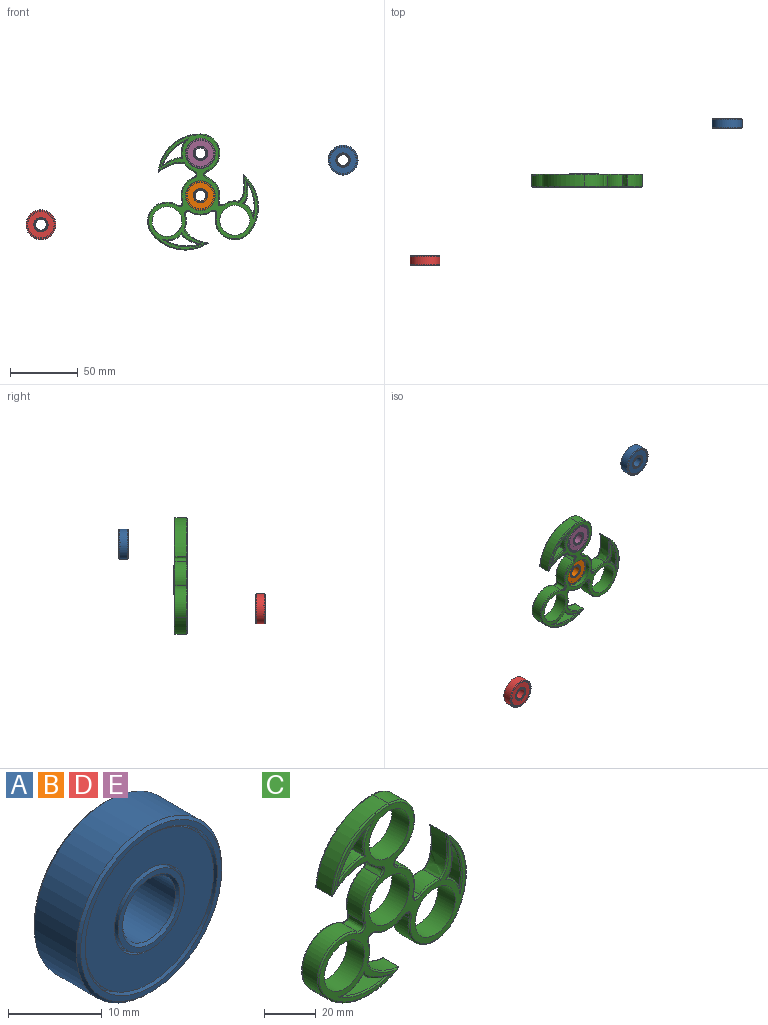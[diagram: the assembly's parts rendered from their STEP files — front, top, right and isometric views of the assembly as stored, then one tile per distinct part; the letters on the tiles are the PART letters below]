
ASSEMBLY  parts=5 mates=2
PART A: 32 faces, bbox 22x7x22 mm
  f0: cylinder r=10mm len=20mm, axis (0,1,0), area 62.8mm2, adj f1,f19
  f1: plane 21.34x21.34mm, normal (0,1,0), area 43.5mm2, adj f0,f21
  f2: cylinder r=11mm len=22mm, axis (0,1,0), area 438.2mm2, adj f20,f21
  f3: plane 21.34x21.34mm, normal (0,-1,0), area 43.5mm2, adj f4,f20
  f4: cylinder r=10mm len=20mm, axis (0,1,0), area 62.8mm2, adj f3,f5
  f5: plane 20x20mm, normal (0,-1,0), area 18.1mm2, adj f4,f6
  f6: cylinder r=9.71mm len=19.42mm, axis (0,1,0), area 44.7mm2, adj f5,f7
  f7: plane 19.42x19.42mm, normal (0,-1,0), area 208.1mm2, adj f6,f8
  f8: cylinder r=5.29mm len=10.58mm, axis (0,1,0), area 24.4mm2, adj f7,f9
  f9: plane 10.58x10.58mm, normal (0,-1,0), area 9.4mm2, adj f8,f10
  f10: cylinder r=5mm len=10mm, axis (0,1,0), area 31.4mm2, adj f9,f11
  f11: plane 10x10mm, normal (0,-1,0), area 19.6mm2, adj f10,f22
  f12: cylinder r=4mm len=8mm, axis (0,1,0), area 159.3mm2, adj f22,f23
  f13: plane 10x10mm, normal (0,1,0), area 19.6mm2, adj f14,f23
  f14: cylinder r=5mm len=10mm, axis (0,1,0), area 31.4mm2, adj f13,f15
  f15: plane 10.58x10.58mm, normal (0,1,0), area 9.4mm2, adj f14,f16
  f16: cylinder r=5.29mm len=10.58mm, axis (0,1,0), area 24.4mm2, adj f15,f17
  f17: plane 19.42x19.42mm, normal (0,1,0), area 208.1mm2, adj f16,f18
  f18: cylinder r=9.71mm len=19.42mm, axis (0,1,0), area 44.7mm2, adj f17,f19
  f19: plane 20x20mm, normal (0,1,0), area 18.1mm2, adj f0,f18
  f20: cone r=11mm half-angle=45deg, axis (0,1,0), area 31.8mm2, adj f2,f3
  f21: cone r=10.67mm half-angle=45deg, axis (0,-1,0), area 31.8mm2, adj f1,f2
  f22: cone r=4.33mm half-angle=45deg, axis (0,-1,0), area 12.2mm2, adj f11,f12
  f23: cone r=4mm half-angle=45deg, axis (0,1,0), area 12.2mm2, adj f12,f13
  f24: cylinder r=8.16mm len=16.32mm, axis (0,1,0), area 48.4mm2, adj f25,f31
  f25: torus R=7.5mm, axis (0,1,0), area 219.3mm2, adj f24,f26
  f26: cylinder r=8.16mm len=16.32mm, axis (0,1,0), area 48.4mm2, adj f25,f27
  f27: plane 16.32x16.32mm, normal (0,-1,0), area 62.1mm2, adj f26,f28
  f28: cylinder r=6.84mm len=13.68mm, axis (0,1,0), area 40.6mm2, adj f27,f29
  f29: torus R=7.5mm, axis (0,1,0), area 153.3mm2, adj f28,f30
  f30: cylinder r=6.84mm len=13.68mm, axis (0,1,0), area 40.6mm2, adj f29,f31
  f31: plane 16.32x16.32mm, normal (0,1,0), area 62.1mm2, adj f24,f30
PART B: same geometry as A
PART C: 87 faces, bbox 85.3x9.5x90.6 mm
  f0: cylinder r=30.84mm len=23.63mm, axis (0,1,0), area 216.9mm2, adj f1,f29,f31,f77
  f1: cylinder r=14.29mm len=11.04mm, axis (0,1,0), area 110.8mm2, adj f0,f29,f31,f79
  f2: cylinder r=30.84mm len=23.07mm, axis (0,1,0), area 214.3mm2, adj f3,f26,f31,f74
  f3: cylinder r=14.29mm len=8.89mm, axis (0,1,0), area 99.4mm2, adj f2,f26,f31,f76
  f4: cylinder r=14.29mm len=27.66mm, axis (0,1,0), area 328.1mm2, adj f5,f27,f39,f60
  f5: cylinder r=30.84mm len=31.09mm, axis (0,1,0), area 384mm2, adj f4,f6,f37,f58
  f6: extruded ~19.01x8.26mm, area 172.9mm2, adj f5,f7,f35,f56
  f7: cylinder r=14.29mm len=8.26mm, axis (0,1,0), area 76.4mm2, adj f6,f8,f33,f54
  f8: extruded ~8.26x4.37mm, area 49.4mm2, adj f7,f9,f32,f53
  f9: cylinder r=14.29mm len=17.94mm, axis (0,1,0), area 181.2mm2, adj f8,f10,f34,f55
  f10: extruded ~8.26x3.92mm, area 50.1mm2, adj f9,f11,f36,f57
  f11: cylinder r=14.29mm len=22.99mm, axis (0,1,0), area 324.4mm2, adj f10,f12,f38,f59
  f12: cylinder r=30.84mm len=41.6mm, axis (0,1,0), area 384mm2, adj f11,f13,f40,f61
  f13: extruded ~17.08x10.46mm, area 172.8mm2, adj f12,f14,f42,f63
  f14: cylinder r=14.29mm len=10.04mm, axis (0,1,0), area 84.7mm2, adj f13,f15,f44,f65
  f15: extruded ~8.26x3.57mm, area 46.5mm2, adj f14,f16,f46,f67
  f16: cylinder r=14.29mm len=15.17mm, axis (0,1,0), area 132mm2, adj f15,f17,f48,f69
  f17: extruded ~8.26x3.72mm, area 50.2mm2, adj f16,f18,f50,f71
  f18: cylinder r=14.29mm len=25.99mm, axis (0,1,0), area 328.1mm2, adj f17,f19,f52,f73
  f19: cylinder r=30.84mm len=41.86mm, axis (0,1,0), area 384mm2, adj f18,f20,f51,f72
  f20: extruded ~19.63x8.26mm, area 173.1mm2, adj f19,f21,f49,f70
  f21: cylinder r=14.29mm len=10.73mm, axis (0,1,0), area 92.9mm2, adj f20,f22,f47,f68
  f22: extruded ~8.26x3.49mm, area 48.5mm2, adj f21,f23,f45,f66
  f23: cylinder r=14.29mm len=17.37mm, axis (0,1,0), area 176.3mm2, adj f22,f27,f43,f64
  f24: cylinder r=30.84mm len=17.36mm, axis (0,1,0), area 218mm2, adj f25,f28,f31,f80
  f25: cylinder r=14.29mm len=12.3mm, axis (0,1,0), area 116mm2, adj f24,f28,f31,f81
  f26: extruded ~14.58x8.89mm, area 136.2mm2, adj f2,f3,f31,f75
  f27: extruded ~8.26x4.37mm, area 49.4mm2, adj f4,f23,f41,f62
  f28: extruded ~13.64x8.89mm, area 132mm2, adj f24,f25,f31,f82
  f29: extruded ~12.59x8.89mm, area 132.9mm2, adj f0,f1,f31,f78
  f30: plane 84.23x80.29mm, normal (0,-1,0), area 1178mm2, adj f53,f54,f55,f56,f57,f58,f59,f60
  f31: plane 84.23x80.29mm, normal (0,1,0), area 1287.4mm2, adj f0,f1,f2,f3,f24,f25,f26,f28
  f32: bspline ~5.77x2.81mm, area 6.5mm2, adj f8,f31,f33,f34
  f33: torus R=13.65mm, axis (0,-1,0), area 9.2mm2, adj f7,f31,f32,f35
  f34: torus R=13.65mm, axis (0,-1,0), area 21.6mm2, adj f9,f31,f32,f36
  f35: bspline ~21.17x8.17mm, area 20.4mm2, adj f6,f31,f33,f37
  f36: bspline ~5.39x4.25mm, area 6.6mm2, adj f10,f31,f34,f38
  f37: torus R=30.2mm, axis (0,-1,0), area 45.2mm2, adj f5,f31,f35,f39
  f38: torus R=13.65mm, axis (0,-1,0), area 38.6mm2, adj f11,f31,f36,f40
  f39: torus R=13.65mm, axis (0,-1,0), area 39mm2, adj f4,f31,f37,f41
  f40: torus R=30.2mm, axis (0,-1,0), area 45.2mm2, adj f12,f31,f38,f42
  f41: bspline ~5.77x2.81mm, area 6.5mm2, adj f27,f31,f39,f43
  f42: bspline ~19.29x12.28mm, area 20.4mm2, adj f13,f31,f40,f44
  f43: torus R=13.65mm, axis (0,-1,0), area 21mm2, adj f23,f31,f41,f45
  f44: torus R=13.65mm, axis (0,-1,0), area 10.2mm2, adj f14,f31,f42,f46
  f45: bspline ~4.56x4.27mm, area 6.4mm2, adj f22,f31,f43,f47
  f46: bspline ~4.64x4.52mm, area 6.1mm2, adj f15,f31,f44,f48
  f47: torus R=13.65mm, axis (0,-1,0), area 11.2mm2, adj f21,f31,f45,f49
  f48: torus R=13.65mm, axis (0,-1,0), area 15.7mm2, adj f16,f31,f46,f50
  f49: bspline ~21.97x6.46mm, area 20.4mm2, adj f20,f31,f47,f51
  f50: bspline ~4.78x4.28mm, area 6.6mm2, adj f17,f31,f48,f52
  f51: torus R=30.2mm, axis (0,-1,0), area 45.2mm2, adj f19,f31,f49,f52
  f52: torus R=13.65mm, axis (0,-1,0), area 39mm2, adj f18,f31,f50,f51
  f53: bspline ~6.02x3.24mm, area 6.5mm2, adj f8,f30,f54,f55
  f54: torus R=13.65mm, axis (0,-1,0), area 9.2mm2, adj f7,f30,f53,f56
  f55: torus R=13.65mm, axis (0,-1,0), area 21.6mm2, adj f9,f30,f53,f57
  f56: bspline ~21.17x8.17mm, area 20.4mm2, adj f6,f30,f54,f58
  f57: bspline ~5.09x3.92mm, area 6.6mm2, adj f10,f30,f55,f59
  f58: torus R=30.2mm, axis (0,-1,0), area 45.2mm2, adj f5,f30,f56,f60
  f59: torus R=13.65mm, axis (0,-1,0), area 38.6mm2, adj f11,f30,f57,f61
  f60: torus R=13.65mm, axis (0,-1,0), area 39mm2, adj f4,f30,f58,f62
  f61: torus R=30.2mm, axis (0,-1,0), area 45.2mm2, adj f12,f30,f59,f63
  f62: bspline ~6.02x3.24mm, area 6.5mm2, adj f27,f30,f60,f64
  f63: bspline ~19.29x12.28mm, area 20.4mm2, adj f13,f30,f61,f65
  f64: torus R=13.65mm, axis (0,-1,0), area 21mm2, adj f23,f30,f62,f66
  f65: torus R=13.65mm, axis (0,-1,0), area 10.2mm2, adj f14,f30,f63,f67
  f66: bspline ~4.55x3.84mm, area 6.4mm2, adj f22,f30,f64,f68
  f67: bspline ~4.72x3.88mm, area 6.1mm2, adj f15,f30,f65,f69
  f68: torus R=13.65mm, axis (0,-1,0), area 11.2mm2, adj f21,f30,f66,f70
  f69: torus R=13.65mm, axis (0,-1,0), area 15.7mm2, adj f16,f30,f67,f71
  f70: bspline ~21.97x6.46mm, area 20.4mm2, adj f20,f30,f68,f72
  f71: bspline ~5.16x3.94mm, area 6.6mm2, adj f17,f30,f69,f73
  f72: torus R=30.2mm, axis (0,-1,0), area 45.2mm2, adj f19,f30,f70,f73
  f73: torus R=13.65mm, axis (0,-1,0), area 39mm2, adj f18,f30,f71,f72
  f74: torus R=31.47mm, axis (0,-1,0), area 27mm2, adj f2,f30,f75,f76
  f75: bspline ~19.09x4.61mm, area 16.9mm2, adj f26,f30,f74,f76
  f76: torus R=13.65mm, axis (0,-1,0), area 12.9mm2, adj f3,f30,f74,f75
  f77: torus R=31.47mm, axis (0,-1,0), area 27.1mm2, adj f0,f30,f78,f79
  f78: bspline ~16.66x10.24mm, area 16.4mm2, adj f29,f30,f77,f79
  f79: torus R=13.65mm, axis (0,-1,0), area 14.2mm2, adj f1,f30,f77,f78
  f80: torus R=31.47mm, axis (0,-1,0), area 27.2mm2, adj f24,f30,f81,f82
  f81: torus R=13.65mm, axis (0,-1,0), area 14.8mm2, adj f25,f30,f80,f82
  f82: bspline ~17.18x7.24mm, area 16.2mm2, adj f28,f30,f80,f81
  f83: cylinder r=11mm len=22mm, axis (0,1,0), area 658.3mm2, adj f30,f31
  f84: cylinder r=11mm len=22mm, axis (0,1,0), area 658.3mm2, adj f30,f31
  f85: cylinder r=11mm len=22mm, axis (0,1,0), area 658.3mm2, adj f30,f31
  f86: cylinder r=11mm len=22mm, axis (0,1,0), area 658.3mm2, adj f30,f31
PART D: same geometry as A
PART E: same geometry as A
PLACE A t=(64.14,30.01,10.27)mm
PLACE B rot(axis=(1,0,0),180deg) t=(-40.89,-10.31,-15.86)mm
PLACE C t=(-40.89,-7.14,-15.86)mm
PLACE D t=(-158.35,-70.64,-37.34)mm
PLACE E t=(-40.89,-13.43,15.26)mm
MATE revolute B.f0 <-> C.f83  axis (0,-1,0) through (-40.89,-7.14,-15.86)mm
MATE revolute C.f4 <-> E.f0  axis (0,-1,0) through (-40.89,-16.67,15.26)mm
